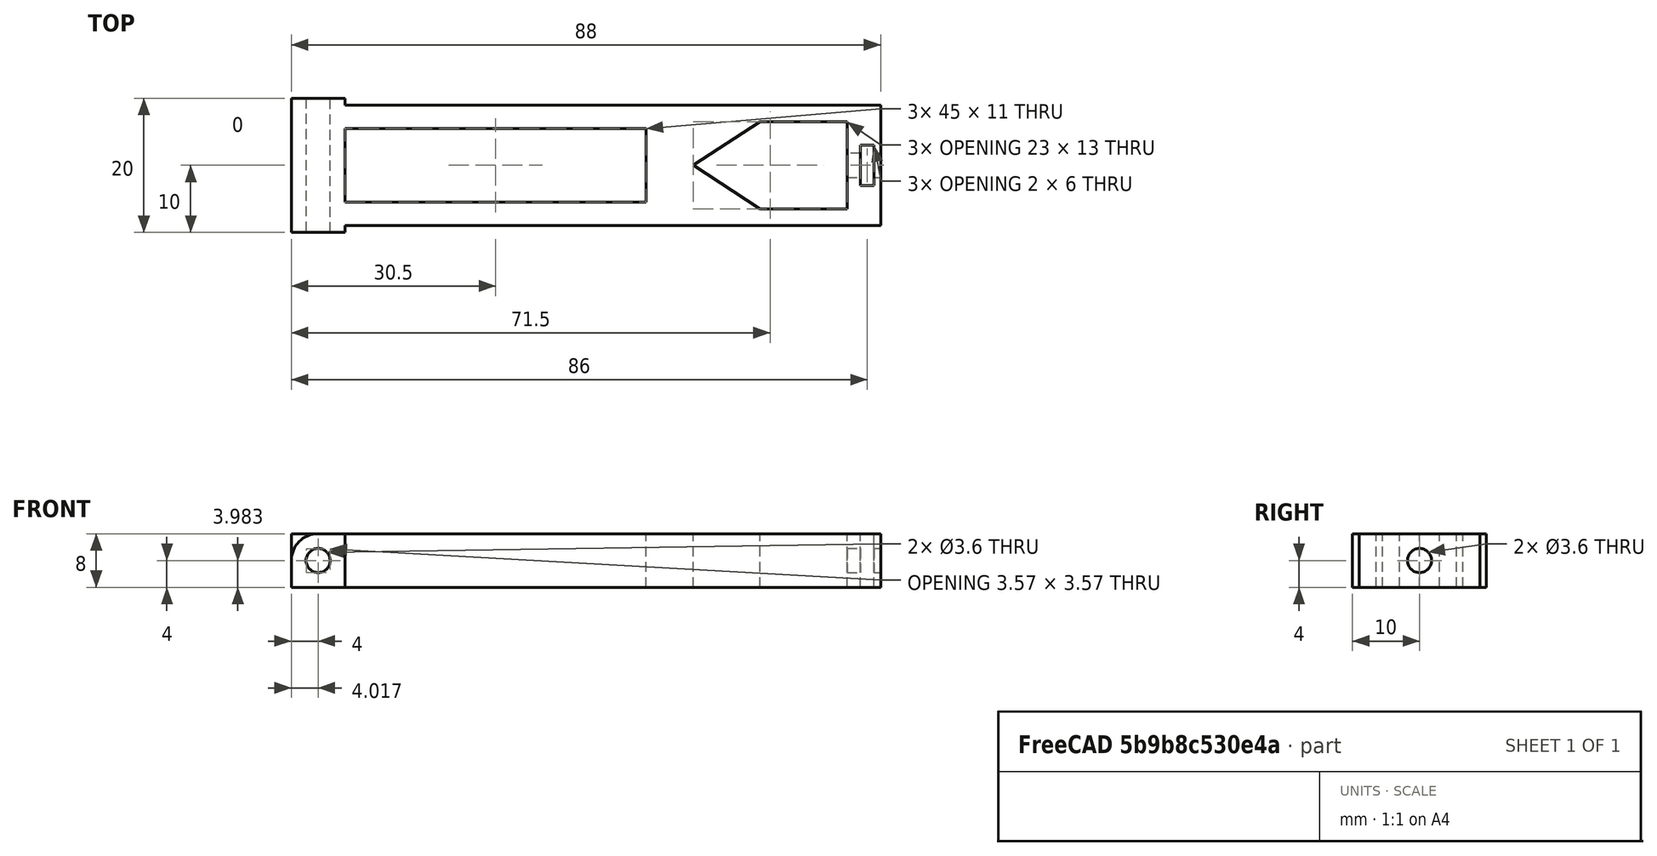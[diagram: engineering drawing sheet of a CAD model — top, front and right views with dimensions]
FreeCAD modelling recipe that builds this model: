
FCSTD DOCUMENT
Label: PenArm
objects: Sketcher::SketchObject×3, PartDesign::Pocket×2, PartDesign::Pad×1, Mesh::Feature×1
note: 7 computed .brp shape members not serialized (recipe doc carries the construction recipe); baked Part::Feature solids carry a one-line shape summary decoded from their .brp

FEATURE [Sketcher::SketchObject] Sketch
  sketch-geometry (27):
    g0: LineSegment StartX=8 StartY=20 StartZ=0 EndX=0 EndY=20 EndZ=0
    g1: LineSegment StartX=0 StartY=20 StartZ=0 EndX=0 EndY=0 EndZ=0
    g2: LineSegment StartX=0 StartY=0 StartZ=0 EndX=8 EndY=0 EndZ=0
    g3: LineSegment StartX=8 StartY=19 StartZ=0 EndX=88 EndY=19 EndZ=0
    g4: LineSegment StartX=88 StartY=19 StartZ=0 EndX=88 EndY=1 EndZ=0
    g5: LineSegment StartX=88 StartY=1 StartZ=0 EndX=8 EndY=1 EndZ=0
    g6: LineSegment StartX=8 StartY=20 StartZ=0 EndX=8 EndY=19 EndZ=0
    g7: LineSegment StartX=8 StartY=1 StartZ=0 EndX=8 EndY=0 EndZ=0
    g8: LineSegment StartX=60 StartY=10 StartZ=0 EndX=70 EndY=16.5 EndZ=0
    g9: LineSegment StartX=70 StartY=16.5 StartZ=0 EndX=83 EndY=16.5 EndZ=0
    g10: LineSegment StartX=83 StartY=16.5 StartZ=0 EndX=83 EndY=3.5 EndZ=0
    g11: LineSegment StartX=83 StartY=3.5 StartZ=0 EndX=70 EndY=3.5 EndZ=0
    g12: LineSegment StartX=70 StartY=3.5 StartZ=0 EndX=60 EndY=10 EndZ=0
    g13: LineSegment [constr] StartX=70 StartY=16.5 StartZ=0 EndX=70 EndY=10 EndZ=0
    g14: LineSegment [constr] StartX=70 StartY=10 StartZ=0 EndX=70 EndY=3.5 EndZ=0
    g15: LineSegment [constr] StartX=70 StartY=10 StartZ=0 EndX=60 EndY=10 EndZ=0
    g16: LineSegment StartX=85 StartY=13.0011 StartZ=0 EndX=87 EndY=13.0011 EndZ=0
    g17: LineSegment StartX=87 StartY=6.99895 StartZ=0 EndX=85 EndY=6.99895 EndZ=0
    g18: LineSegment StartX=85 StartY=6.99895 StartZ=0 EndX=85 EndY=13.0011 EndZ=0
    g19: LineSegment StartX=87 StartY=13.0011 StartZ=0 EndX=87 EndY=10 EndZ=0
    g20: LineSegment StartX=87 StartY=10 StartZ=0 EndX=87 EndY=6.99895 EndZ=0
    g21: LineSegment StartX=53 StartY=15.5 StartZ=0 EndX=8 EndY=15.5 EndZ=0
    g22: LineSegment StartX=8 StartY=4.5 StartZ=0 EndX=53 EndY=4.5 EndZ=0
    g23: LineSegment StartX=53 StartY=4.5 StartZ=0 EndX=53 EndY=15.5 EndZ=0
    g24: LineSegment [constr] StartX=8 StartY=19 StartZ=0 EndX=8 EndY=15.5 EndZ=0
    g25: LineSegment [constr] StartX=8 StartY=1 StartZ=0 EndX=8 EndY=4.5 EndZ=0
    g26: LineSegment StartX=8 StartY=15.5 StartZ=0 EndX=8 EndY=4.5 EndZ=0
  constraints (77):
    c: Coincident(g0,g1)
    c: Coincident(g1,g2)
    c: Horizontal(g0)
    c: Horizontal(g2)
    c: Vertical(g1)
    c: Coincident(g3,g4)
    c: Coincident(g4,g5)
    c: Horizontal(g3)
    c: Horizontal(g5)
    c: Vertical(g4)
    c: Coincident(g6,g0)
    c: Coincident(g6,g3)
    c: Vertical(g6)
    c: Coincident(g7,g5)
    c: Coincident(g7,g2)
    c: Vertical(g7)
    c: Coincident(g8,g9)
    c: Horizontal(g9)
    c: Coincident(g9,g10)
    c: Coincident(g10,g11)
    c: Coincident(g11,g12)
    c: Coincident(g12,g8)
    c: Horizontal(g11)
    c: Vertical(g10)
    c: Coincident(g13,g8)
    c: Coincident(g13,g14)
    c: Coincident(g14,g11)
    c: Coincident(g15,g13)
    c: Coincident(g15,g8)
    c: Horizontal(g15)
    c: Vertical(g13)
    c: Vertical(g14)
    c: Equal(g14,g13)
    c: DistanceX(g2) = 8
    c: DistanceY(g4) = -18
    c: DistanceY(g1) = -20
    c: Equal(g6,g7)
    c: DistanceX(g5) = -80
    c: DistanceY(g10) = -13
    c: DistanceX(g8,g11) = 10
    c: DistanceX(g11) = -13
    c: DistanceX(g8) = 60
    c: DistanceY(g8) = 10
    c: Equal(g2,g0)
    c: Coincident(g17,g18)
    c: Coincident(g18,g16)
    c: Horizontal(g16)
    c: Horizontal(g17)
    c: Vertical(g18)
    c: Coincident(g19,g16)
    c: Vertical(g19)
    c: Coincident(g19,g20)
    c: Coincident(g20,g17)
    c: Vertical(g20)
    c: Equal(g20,g19)
    c: DistanceX(g16) = 2
    c: DistanceY(g16,g17) = -6.00211
    c: DistanceX(g19) = 87
    c: DistanceY(g19) = 10
    c: Coincident(g22,g23)
    c: Coincident(g23,g21)
    c: Horizontal(g21)
    c: Horizontal(g22)
    c: Vertical(g23)
    c: Coincident(g24,g3)
    c: Coincident(g24,g21)
    c: Vertical(g24)
    c: Equal(g24,g25)
    c: DistanceX(g21) = -45
    c: DistanceY(g23) = 11
    c: Coincident(g25,g5)
    c: Coincident(g25,g22)
    c: Coincident(g26,g21)
    c: Coincident(g26,g22)
    c: Vertical(g26)
    c: DistanceX(g1) = 0
    c: DistanceY(g1) = 0
FEATURE [PartDesign::Pad] Pad
  Length = 8
  MirroredExtent = false
  Sketch = -> Sketch
FEATURE [Sketcher::SketchObject] Sketch001
  Placement = pos=(0,0,0) rot=(1,0,0;1.5708rad)
  Support = -> Pad [Face4]
  sketch-geometry (8):
    g0: Circle CenterX=4 CenterY=4 CenterZ=0 NormalX=0 NormalY=0 NormalZ=1 Radius=1.8
    g1: LineSegment StartX=4 StartY=8 StartZ=0 EndX=4 EndY=9 EndZ=0
    g2: LineSegment StartX=4 StartY=9 StartZ=0 EndX=-1 EndY=9 EndZ=0
    g3: LineSegment StartX=-1 StartY=9 StartZ=0 EndX=-1 EndY=4 EndZ=0
    g4: LineSegment StartX=-1 StartY=4 StartZ=0 EndX=0 EndY=4 EndZ=0
    g5: LineSegment [constr] StartX=4 StartY=8 StartZ=0 EndX=4 EndY=4 EndZ=0
    g6: LineSegment [constr] StartX=4 StartY=4 StartZ=0 EndX=0 EndY=4 EndZ=0
    g7: ArcOfCircle CenterX=4 CenterY=4 CenterZ=0 NormalX=0 NormalY=0 NormalZ=1 Radius=4 StartAngle=1.5708 EndAngle=3.14159
  constraints (22):
    c: DistanceX(g0) = 4
    c: DistanceY(g0) = 4
    c: Radius(g0) = 1.8
    c: Vertical(g1)
    c: Coincident(g1,g2)
    c: Horizontal(g2)
    c: Coincident(g2,g3)
    c: Vertical(g3)
    c: Coincident(g3,g4)
    c: Horizontal(g4)
    c: DistanceY(g1) = 1
    c: Vertical(g5)
    c: Coincident(g5,g6)
    c: Coincident(g5,g0)
    c: Horizontal(g6)
    c: DistanceX(g6) = -4
    c: Coincident(g7,g4)
    c: Coincident(g7,g1)
    c: Coincident(g5,g1)
    c: Coincident(g7,g0)
    c: Coincident(g4,g6)
    c: Equal(g1,g4)
FEATURE [PartDesign::Pocket] Pocket
  Length = 20
  Sketch = -> Sketch001
  Type = 0
FEATURE [Sketcher::SketchObject] Sketch002
  Placement = pos=(88,0,0) rot=(0.57735,0.57735,0.57735;2.0944rad)
  Support = -> Pocket [Face9]
  sketch-geometry (1):
    g0: Circle CenterX=10 CenterY=4 CenterZ=0 NormalX=0 NormalY=0 NormalZ=1 Radius=1.8
  constraints (3):
    c: DistanceX(g0) = 10
    c: DistanceY(g0) = 4
    c: Radius(g0) = 1.8
FEATURE [PartDesign::Pocket] Pocket001
  Length = 7
  Sketch = -> Sketch002
  Type = 0
FEATURE [Mesh::Feature] Pen_Arm_Top_springy_Longer
